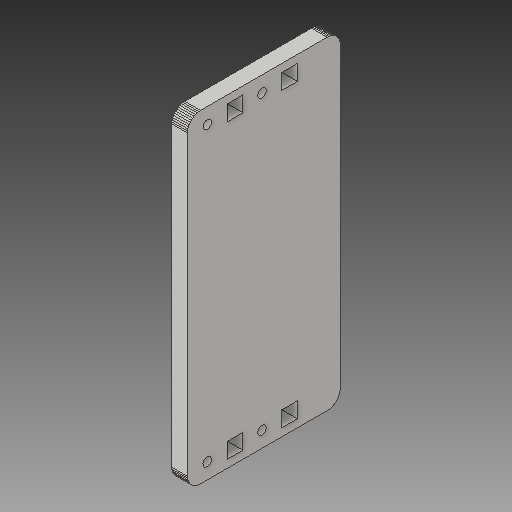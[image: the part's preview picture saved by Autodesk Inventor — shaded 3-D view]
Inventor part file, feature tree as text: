
AUTODESK INVENTOR PART (.ipt)
format: ipt  version: 2018 (Build 220112000, 112)  size: 343,040 bytes
history: native  units: mm
features: other x6, sketch x2, hole x1, reference x1
ambient origin geometry x8: Origin, YZ Plane, XZ Plane, XY Plane, X Axis, Y Axis, Z Axis, Center Point
bodies: Solid1 (feature_tree)
feature tree (10):
  other  "X Axis Brace.ipt"
  hole  "Hole1"  [1 undecoded]
  other  "Solid1::X Axis Brace.ipt"
  other  "TaggingFeature1"
  sketch  "Sketch1"  dims[d0=10.0mm]
  sketch  "Sketch2"  dims[d1=3.3mm d2=6.0mm d3=4.0mm d4=2.0mm d5=90.0deg d6=8.0mm d7=20.594885mm]
  reference  "Reference1"
  parser-record x1  (decoder bookkeeping rows leaked as tree rows — omitted from the tree; the rows remain in map.json)
  other  "Assembly33.iam"
  other  "X Axis Brace:1"
note: 1 required parameter value undecoded (feature->parameter linkage not recoverable at this tier; creation-order binding heuristic only, values carry confidence <= 0.55)
note: 1 file-system path scrubbed to <path> (originals preserved in map.json)
